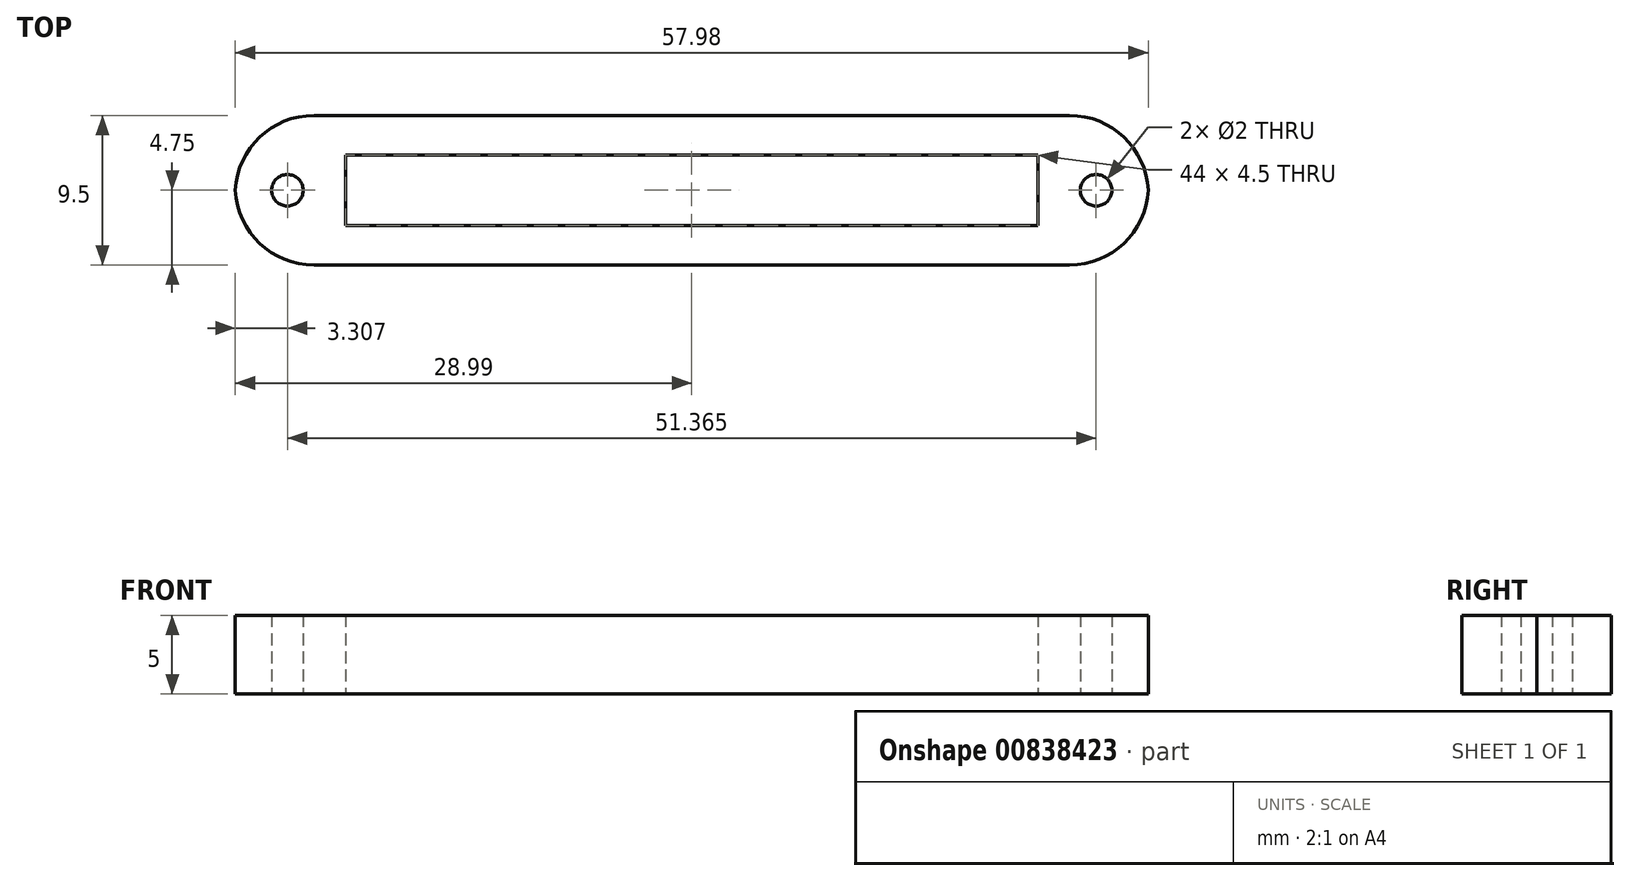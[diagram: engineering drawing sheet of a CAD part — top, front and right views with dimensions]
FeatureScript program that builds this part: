
annotation { "Feature Type Name" : "Feature", "Feature Type Description" : "" }
export const myFeature = defineFeature(function(context is Context, id is Id, definition is map)
    precondition{}
    {
        {
            var Q0;
            Q0=qCreatedBy(makeId("Top.planeOp"),FACE);
            var sketch = newSketch(context, id + "F0", { "sketchPlane" : qUnion([Q0])});
            skLineSegment(sketch, "E0.bottom", {"start": v(29, -4.75) * mm, "end": v(-29, -4.75) * mm});
            skLineSegment(sketch, "E0.top", {"start": v(29, 4.75) * mm, "end": v(-29, 4.75) * mm});
            skLineSegment(sketch, "E0.left", {"start": v(29, -4.75) * mm, "end": v(29, 4.75) * mm});
            skLineSegment(sketch, "E0.right", {"start": v(-29, -4.75) * mm, "end": v(-29, 4.75) * mm});
            skPoint(sketch, "E0.middle", {"position": v(0, 0) * mm});
            skLineSegment(sketch, "E1.bottom", {"start": v(22, -2.25) * mm, "end": v(-22, -2.25) * mm});
            skLineSegment(sketch, "E1.top", {"start": v(22, 2.25) * mm, "end": v(-22, 2.25) * mm});
            skLineSegment(sketch, "E1.left", {"start": v(22, -2.25) * mm, "end": v(22, 2.25) * mm});
            skLineSegment(sketch, "E1.right", {"start": v(-22, -2.25) * mm, "end": v(-22, 2.25) * mm});
            skCircle(sketch, "E2", {"center": v(-25.68, 0) * mm, "radius": 1 * mm});
            skCircle(sketch, "E3.MirrorC", {"center": v(25.68, 0) * mm, "radius": 1 * mm});
            skSolve(sketch);
        }
        {
            var Q0;
            Q0=makeQuery(id+"F0.imprint","IMPRINT",FACE,{"disambiguationData":[TD([[makeQuery(id+"F0.imprint","IMPRINT",EDGE,{"derivedFrom":sQuery(id+"F0.wireOp",EDGE,"E0.bottom")}),-1.0]])]});
            extrude(context, id + "F1", {"entities" : qUnion([Q0]), "depth" : 5 * mm, "offsetDistance" : 25 * mm});
        }
        {
            var Q0;
            Q0=makeQuery(id+"F1.opExtrude","SWEPT_EDGE",EDGE,{"disambiguationData":[OSD([sQuery(id+"F0.wireOp",EDGE,"E0.bottom"),sQuery(id+"F0.wireOp",EDGE,"E0.left")])]});
            var Q1;
            Q1=makeQuery(id+"F1.opExtrude","SWEPT_EDGE",EDGE,{"disambiguationData":[OSD([sQuery(id+"F0.wireOp",EDGE,"E0.top"),sQuery(id+"F0.wireOp",EDGE,"E0.left")])]});
            var Q2;
            Q2=makeQuery(id+"F1.opExtrude","SWEPT_EDGE",EDGE,{"disambiguationData":[OSD([sQuery(id+"F0.wireOp",EDGE,"E0.top"),sQuery(id+"F0.wireOp",EDGE,"E0.right")])]});
            var Q3;
            Q3=makeQuery(id+"F1.opExtrude","SWEPT_EDGE",EDGE,{"disambiguationData":[OSD([sQuery(id+"F0.wireOp",EDGE,"E0.bottom"),sQuery(id+"F0.wireOp",EDGE,"E0.right")])]});
            fillet(context, id + "F2", {"entities" : qUnion([Q0, Q1, Q2, Q3]), "radius" : 5 * mm, "tangentPropagation" : true, "allowEdgeOverflow" : false});
        }
    });
